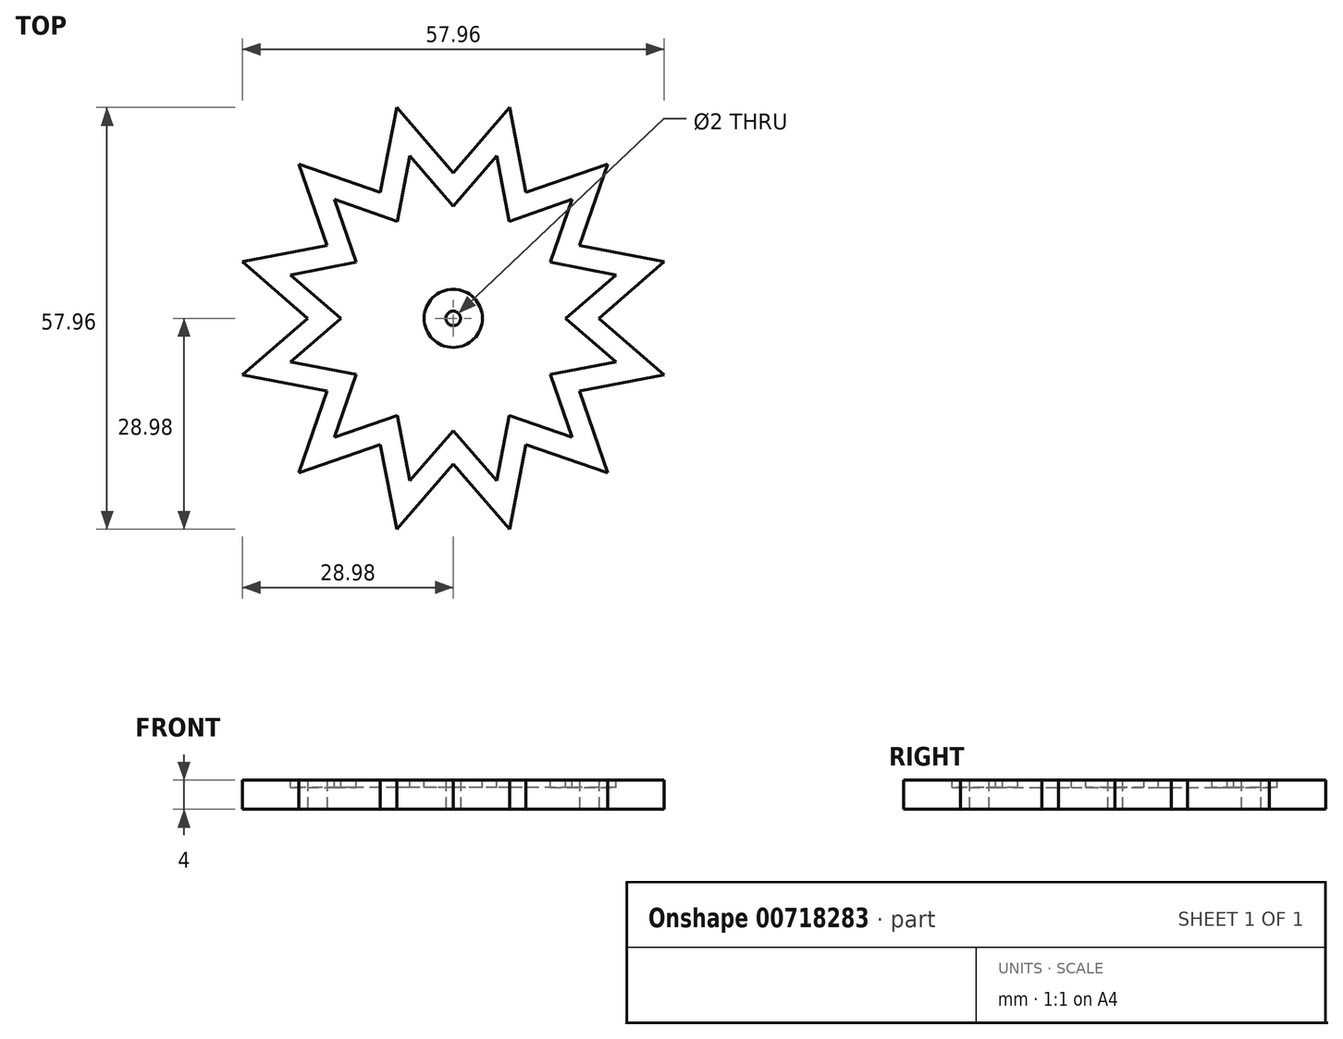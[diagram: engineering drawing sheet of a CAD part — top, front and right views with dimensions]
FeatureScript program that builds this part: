
annotation { "Feature Type Name" : "Feature", "Feature Type Description" : "" }
export const myFeature = defineFeature(function(context is Context, id is Id, definition is map)
    precondition{}
    {
        {
            var Q0;
            Q0=qCreatedBy(makeId("Top.planeOp"),FACE);
            var sketch = newSketch(context, id + "F0", { "sketchPlane" : qUnion([Q0])});
            skCircle(sketch, "E0", {"center": v(0, 0) * mm, "radius": 20 * mm, "construction": true});
            skLineSegment(sketch, "E1", {"start": v(0, 0) * mm, "end": v(0, 20) * mm, "construction": true});
            skLineSegment(sketch, "E2", {"start": v(0, 0) * mm, "end": v(10, 17.32) * mm, "construction": true});
            skCircle(sketch, "E3", {"center": v(0, 0) * mm, "radius": 30 * mm, "construction": true});
            skLineSegment(sketch, "E4", {"start": v(0, 0) * mm, "end": v(7.76, 28.98) * mm, "construction": true});
            skLineSegment(sketch, "E5", {"start": v(0, 20) * mm, "end": v(7.76, 28.98) * mm});
            skLineSegment(sketch, "E6", {"start": v(7.76, 28.98) * mm, "end": v(10, 17.32) * mm});
            skLineSegment(sketch, "E7.1.0", {"start": v(-10, 17.32) * mm, "end": v(-7.76, 28.98) * mm});
            skLineSegment(sketch, "E7.1.1", {"start": v(-7.76, 28.98) * mm, "end": v(0, 20) * mm});
            skLineSegment(sketch, "E7.2.0", {"start": v(-17.32, 10) * mm, "end": v(-21.21, 21.21) * mm});
            skLineSegment(sketch, "E7.2.1", {"start": v(-21.21, 21.21) * mm, "end": v(-10, 17.32) * mm});
            skLineSegment(sketch, "E7.3.0", {"start": v(-20, 0) * mm, "end": v(-28.98, 7.76) * mm});
            skLineSegment(sketch, "E7.3.1", {"start": v(-28.98, 7.76) * mm, "end": v(-17.32, 10) * mm});
            skLineSegment(sketch, "E7.4.0", {"start": v(-17.32, -10) * mm, "end": v(-28.98, -7.76) * mm});
            skLineSegment(sketch, "E7.4.1", {"start": v(-28.98, -7.76) * mm, "end": v(-20, 0) * mm});
            skLineSegment(sketch, "E7.5.0", {"start": v(-10, -17.32) * mm, "end": v(-21.21, -21.21) * mm});
            skLineSegment(sketch, "E7.5.1", {"start": v(-21.21, -21.21) * mm, "end": v(-17.32, -10) * mm});
            skLineSegment(sketch, "E7.6.0", {"start": v(0, -20) * mm, "end": v(-7.76, -28.98) * mm});
            skLineSegment(sketch, "E7.6.1", {"start": v(-7.76, -28.98) * mm, "end": v(-10, -17.32) * mm});
            skLineSegment(sketch, "E7.7.0", {"start": v(10, -17.32) * mm, "end": v(7.76, -28.98) * mm});
            skLineSegment(sketch, "E7.7.1", {"start": v(7.76, -28.98) * mm, "end": v(0, -20) * mm});
            skLineSegment(sketch, "E7.8.0", {"start": v(17.32, -10) * mm, "end": v(21.21, -21.21) * mm});
            skLineSegment(sketch, "E7.8.1", {"start": v(21.21, -21.21) * mm, "end": v(10, -17.32) * mm});
            skLineSegment(sketch, "E7.9.0", {"start": v(20, 0) * mm, "end": v(28.98, -7.76) * mm});
            skLineSegment(sketch, "E7.9.1", {"start": v(28.98, -7.76) * mm, "end": v(17.32, -10) * mm});
            skLineSegment(sketch, "E7.10.0", {"start": v(17.32, 10) * mm, "end": v(28.98, 7.76) * mm});
            skLineSegment(sketch, "E7.10.1", {"start": v(28.98, 7.76) * mm, "end": v(20, 0) * mm});
            skLineSegment(sketch, "E7.11.0", {"start": v(10, 17.32) * mm, "end": v(21.21, 21.21) * mm});
            skLineSegment(sketch, "E7.11.1", {"start": v(21.21, 21.21) * mm, "end": v(17.32, 10) * mm});
            skCircle(sketch, "E8", {"center": v(0, 0) * mm, "radius": 1 * mm});
            skSolve(sketch);
        }
        {
            var Q0;
            Q0=makeQuery(id+"F0.imprint","IMPRINT",FACE,{"disambiguationData":[TD([[makeQuery(id+"F0.imprint","IMPRINT",EDGE,{"derivedFrom":sQuery(id+"F0.wireOp",EDGE,"E5")}),-1.0]])]});
            extrude(context, id + "F1", {"entities" : qUnion([Q0]), "depth" : 4 * mm, "offsetDistance" : 25 * mm});
        }
        {
            var Q0;
            Q0=makeQuery(id+"F1.opExtrude","CAP_FACE",FACE,{"disambiguationData":[OSD([sQuery(id+"F0.wireOp",EDGE,"E5"),sQuery(id+"F0.wireOp",EDGE,"E6"),sQuery(id+"F0.wireOp",EDGE,"E7.1.0"),sQuery(id+"F0.wireOp",EDGE,"E7.1.1"),sQuery(id+"F0.wireOp",EDGE,"E7.2.0"),sQuery(id+"F0.wireOp",EDGE,"E7.2.1"),sQuery(id+"F0.wireOp",EDGE,"E7.3.0"),sQuery(id+"F0.wireOp",EDGE,"E7.3.1"),sQuery(id+"F0.wireOp",EDGE,"E7.4.0"),sQuery(id+"F0.wireOp",EDGE,"E7.4.1"),sQuery(id+"F0.wireOp",EDGE,"E7.5.0"),sQuery(id+"F0.wireOp",EDGE,"E7.5.1"),sQuery(id+"F0.wireOp",EDGE,"E7.6.0"),sQuery(id+"F0.wireOp",EDGE,"E7.6.1"),sQuery(id+"F0.wireOp",EDGE,"E7.7.0"),sQuery(id+"F0.wireOp",EDGE,"E7.7.1"),sQuery(id+"F0.wireOp",EDGE,"E7.8.0"),sQuery(id+"F0.wireOp",EDGE,"E7.8.1"),sQuery(id+"F0.wireOp",EDGE,"E7.9.0"),sQuery(id+"F0.wireOp",EDGE,"E7.9.1"),sQuery(id+"F0.wireOp",EDGE,"E7.10.0"),sQuery(id+"F0.wireOp",EDGE,"E7.10.1"),sQuery(id+"F0.wireOp",EDGE,"E7.11.0"),sQuery(id+"F0.wireOp",EDGE,"E7.11.1"),sQuery(id+"F0.wireOp",EDGE,"E8")])],"isStart":false});
            var sketch = newSketch(context, id + "F2", { "sketchPlane" : qUnion([Q0])});
            skCircle(sketch, "E9.0", {"center": v(0, 0) * mm, "radius": 4 * mm});
            skLineSegment(sketch, "E10.0", {"start": v(-16.35, -16.35) * mm, "end": v(-7.7, -13.35) * mm});
            skLineSegment(sketch, "E10.1", {"start": v(13.35, 7.7) * mm, "end": v(16.35, 16.35) * mm});
            skLineSegment(sketch, "E10.2", {"start": v(22.33, 5.98) * mm, "end": v(13.35, 7.7) * mm});
            skLineSegment(sketch, "E10.3", {"start": v(15.41, 0) * mm, "end": v(22.33, 5.98) * mm});
            skLineSegment(sketch, "E10.4", {"start": v(22.33, -5.98) * mm, "end": v(15.41, 0) * mm});
            skLineSegment(sketch, "E10.5", {"start": v(13.35, -7.7) * mm, "end": v(22.33, -5.98) * mm});
            skLineSegment(sketch, "E10.6", {"start": v(16.35, -16.35) * mm, "end": v(13.35, -7.7) * mm});
            skLineSegment(sketch, "E10.7", {"start": v(-5.98, -22.33) * mm, "end": v(0, -15.41) * mm});
            skLineSegment(sketch, "E10.8", {"start": v(0, -15.41) * mm, "end": v(5.98, -22.33) * mm});
            skLineSegment(sketch, "E10.9", {"start": v(5.98, -22.33) * mm, "end": v(7.7, -13.35) * mm});
            skLineSegment(sketch, "E10.10", {"start": v(7.7, -13.35) * mm, "end": v(16.35, -16.35) * mm});
            skLineSegment(sketch, "E10.11", {"start": v(16.35, 16.35) * mm, "end": v(7.7, 13.35) * mm});
            skLineSegment(sketch, "E10.12", {"start": v(-7.7, -13.35) * mm, "end": v(-5.98, -22.33) * mm});
            skLineSegment(sketch, "E10.13", {"start": v(7.7, 13.35) * mm, "end": v(5.98, 22.33) * mm});
            skLineSegment(sketch, "E10.14", {"start": v(5.98, 22.33) * mm, "end": v(0, 15.41) * mm});
            skLineSegment(sketch, "E10.15", {"start": v(0, 15.41) * mm, "end": v(-5.98, 22.33) * mm});
            skLineSegment(sketch, "E10.16", {"start": v(-5.98, 22.33) * mm, "end": v(-7.7, 13.35) * mm});
            skLineSegment(sketch, "E10.17", {"start": v(-7.7, 13.35) * mm, "end": v(-16.35, 16.35) * mm});
            skLineSegment(sketch, "E10.18", {"start": v(-16.35, 16.35) * mm, "end": v(-13.35, 7.7) * mm});
            skLineSegment(sketch, "E10.19", {"start": v(-13.35, 7.7) * mm, "end": v(-22.33, 5.98) * mm});
            skLineSegment(sketch, "E10.20", {"start": v(-22.33, 5.98) * mm, "end": v(-15.41, 0) * mm});
            skLineSegment(sketch, "E10.21", {"start": v(-15.41, 0) * mm, "end": v(-22.33, -5.98) * mm});
            skLineSegment(sketch, "E10.22", {"start": v(-22.33, -5.98) * mm, "end": v(-13.35, -7.7) * mm});
            skLineSegment(sketch, "E10.23", {"start": v(-13.35, -7.7) * mm, "end": v(-16.35, -16.35) * mm});
            skSolve(sketch);
        }
        {
            var Q0;
            Q0=makeQuery(id+"F2.imprint","IMPRINT",FACE,{"disambiguationData":[TD([[makeQuery(id+"F2.imprint","IMPRINT",EDGE,{"derivedFrom":sQuery(id+"F2.wireOp",EDGE,"E9.0")}),-1.0]])]});
            extrude(context, id + "F3", {"entities" : qUnion([Q0]), "operationType" : NewBodyOperationType.REMOVE, "oppositeDirection" : true, "depth" : 1 * mm, "offsetDistance" : 25 * mm});
        }
    });
